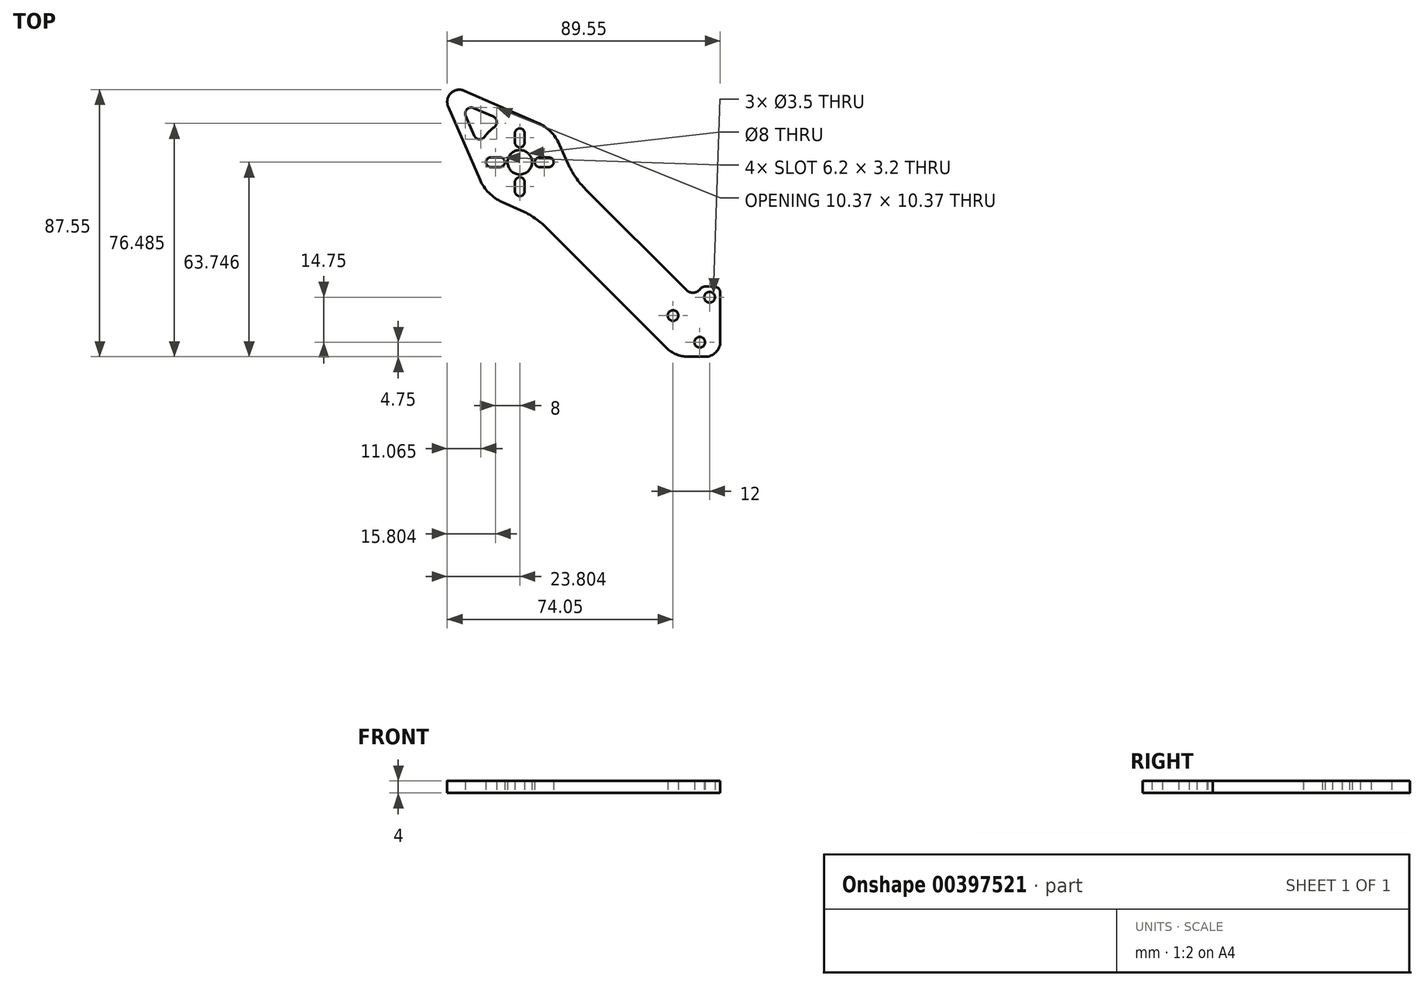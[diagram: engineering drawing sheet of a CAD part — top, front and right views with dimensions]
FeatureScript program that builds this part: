
annotation { "Feature Type Name" : "Feature", "Feature Type Description" : "" }
export const myFeature = defineFeature(function(context is Context, id is Id, definition is map)
    precondition{}
    {
        {
            var Q0;
            Q0=qCreatedBy(makeId("Top.planeOp"),FACE);
            var sketch = newSketch(context, id + "F0", { "sketchPlane" : qUnion([Q0])});
            skCircle(sketch, "E0", {"center": v(0, 0) * mm, "radius": 105 * mm, "construction": true});
            skCircle(sketch, "E1", {"center": v(-15.25, 15.25) * mm, "radius": 1.75 * mm});
            skLineSegment(sketch, "E2", {"start": v(-19.09, 10.5) * mm, "end": v(-13.5, 10.5) * mm});
            skCircle(sketch, "E3", {"center": v(-24, 24) * mm, "radius": 1.75 * mm});
            skLineSegment(sketch, "E4", {"start": v(0, 0) * mm, "end": v(-74.25, 74.25) * mm, "construction": true});
            skLineSegment(sketch, "E5", {"start": v(-65.32, 52.6) * mm, "end": v(-26.16, 13.43) * mm});
            skLineSegment(sketch, "E6", {"start": v(-52.6, 65.32) * mm, "end": v(-19.63, 32.36) * mm});
            skPoint(sketch, "E7.visualSharp", {"position": v(-23.23, 10.5) * mm});
            skArc(sketch, "E7.filletArc", {"start": v(-26.16, 13.43) * mm, "mid": v(-22.91, 11.26) * mm, "end": v(-19.09, 10.5) * mm});
            skCircle(sketch, "E8", {"center": v(-74.25, 74.25) * mm, "radius": 4 * mm});
            skArc(sketch, "E9", {"start": v(-87.31, 68.56) * mm, "mid": v(-84.37, 64.22) * mm, "end": v(-80.06, 61.24) * mm});
            skArc(sketch, "E10", {"start": v(-92.45, 97.71) * mm, "mid": v(-96.87, 96.87) * mm, "end": v(-97.71, 92.45) * mm});
            skLineSegment(sketch, "E11", {"start": v(-94.05, 94.05) * mm, "end": v(-74.25, 74.25) * mm, "construction": true});
            skLineSegment(sketch, "E12", {"start": v(-92.45, 97.71) * mm, "end": v(-68.56, 87.31) * mm});
            skLineSegment(sketch, "E13", {"start": v(-87.31, 68.56) * mm, "end": v(-97.71, 92.45) * mm});
            skLineSegment(sketch, "E14", {"start": v(-61.24, 80.06) * mm, "end": v(-58.46, 73.85) * mm});
            skLineSegment(sketch, "E15", {"start": v(-80.06, 61.24) * mm, "end": v(-73.85, 58.46) * mm});
            skArc(sketch, "E16.trimOffspring", {"start": v(-61.24, 80.06) * mm, "mid": v(-64.22, 84.37) * mm, "end": v(-68.56, 87.31) * mm});
            skPoint(sketch, "E17.center.orphan", {"position": v(-54.45, 54.45) * mm});
            skLineSegment(sketch, "E18", {"start": v(-74.25, 74.25) * mm, "end": v(-74.25, 80.75) * mm, "construction": true});
            skLineSegment(sketch, "E19", {"start": v(-74.25, 80.75) * mm, "end": v(-74.25, 83.75) * mm, "construction": true});
            skLineSegment(sketch, "E20.1.0", {"start": v(-80.75, 74.25) * mm, "end": v(-83.75, 74.25) * mm, "construction": true});
            skLineSegment(sketch, "E20.2.0", {"start": v(-74.25, 67.75) * mm, "end": v(-74.25, 64.75) * mm, "construction": true});
            skLineSegment(sketch, "E20.3.0", {"start": v(-67.75, 74.25) * mm, "end": v(-64.75, 74.25) * mm, "construction": true});
            skArc(sketch, "E21.0.startCap", {"start": v(-72.65, 80.75) * mm, "mid": v(-74.25, 79.15) * mm, "end": v(-75.85, 80.75) * mm});
            skArc(sketch, "E21.0.endCap", {"start": v(-75.85, 83.75) * mm, "mid": v(-74.25, 85.35) * mm, "end": v(-72.65, 83.75) * mm});
            skLineSegment(sketch, "E21.0.left", {"start": v(-75.85, 80.75) * mm, "end": v(-75.85, 83.75) * mm});
            skLineSegment(sketch, "E21.0.right", {"start": v(-72.65, 80.75) * mm, "end": v(-72.65, 83.75) * mm});
            skArc(sketch, "E22.0.startCap", {"start": v(-80.75, 75.85) * mm, "mid": v(-79.15, 74.25) * mm, "end": v(-80.75, 72.65) * mm});
            skArc(sketch, "E22.0.endCap", {"start": v(-83.75, 72.65) * mm, "mid": v(-85.35, 74.25) * mm, "end": v(-83.75, 75.85) * mm});
            skLineSegment(sketch, "E22.0.left", {"start": v(-80.75, 72.65) * mm, "end": v(-83.75, 72.65) * mm});
            skLineSegment(sketch, "E22.0.right", {"start": v(-80.75, 75.85) * mm, "end": v(-83.75, 75.85) * mm});
            skArc(sketch, "E22.1.startCap", {"start": v(-75.85, 67.75) * mm, "mid": v(-74.25, 69.35) * mm, "end": v(-72.65, 67.75) * mm});
            skArc(sketch, "E22.1.endCap", {"start": v(-72.65, 64.75) * mm, "mid": v(-74.25, 63.15) * mm, "end": v(-75.85, 64.75) * mm});
            skLineSegment(sketch, "E22.1.left", {"start": v(-72.65, 67.75) * mm, "end": v(-72.65, 64.75) * mm});
            skLineSegment(sketch, "E22.1.right", {"start": v(-75.85, 67.75) * mm, "end": v(-75.85, 64.75) * mm});
            skArc(sketch, "E22.2.startCap", {"start": v(-67.75, 72.65) * mm, "mid": v(-69.35, 74.25) * mm, "end": v(-67.75, 75.85) * mm});
            skArc(sketch, "E22.2.endCap", {"start": v(-64.75, 75.85) * mm, "mid": v(-63.15, 74.25) * mm, "end": v(-64.75, 72.65) * mm});
            skLineSegment(sketch, "E22.2.left", {"start": v(-67.75, 75.85) * mm, "end": v(-64.75, 75.85) * mm});
            skLineSegment(sketch, "E22.2.right", {"start": v(-67.75, 72.65) * mm, "end": v(-64.75, 72.65) * mm});
            skArc(sketch, "E23", {"start": v(-82.61, 85.78) * mm, "mid": v(-84.32, 84.32) * mm, "end": v(-85.78, 82.61) * mm});
            skLineSegment(sketch, "E24.0", {"start": v(-89.23, 83) * mm, "end": v(-92.02, 89.38) * mm});
            skLineSegment(sketch, "E25.0", {"start": v(-89.38, 92.02) * mm, "end": v(-83, 89.23) * mm});
            skArc(sketch, "E26.filletArc", {"start": v(-89.38, 92.02) * mm, "mid": v(-91.6, 91.6) * mm, "end": v(-92.02, 89.38) * mm});
            skPoint(sketch, "E27.visualSharp", {"position": v(-87.6, 79.23) * mm});
            skArc(sketch, "E27.filletArc", {"start": v(-89.23, 83) * mm, "mid": v(-87.62, 81.8) * mm, "end": v(-85.78, 82.61) * mm});
            skPoint(sketch, "E28.visualSharp", {"position": v(-79.23, 87.6) * mm});
            skArc(sketch, "E28.filletArc", {"start": v(-82.61, 85.78) * mm, "mid": v(-81.8, 87.62) * mm, "end": v(-83, 89.23) * mm});
            skPoint(sketch, "E29.visualSharp", {"position": v(-69.04, 56.31) * mm});
            skArc(sketch, "E29.filletArc", {"start": v(-65.32, 52.6) * mm, "mid": v(-69.31, 55.92) * mm, "end": v(-73.85, 58.46) * mm});
            skPoint(sketch, "E30.visualSharp", {"position": v(-56.31, 69.04) * mm});
            skArc(sketch, "E30.filletArc", {"start": v(-58.46, 73.85) * mm, "mid": v(-55.92, 69.31) * mm, "end": v(-52.6, 65.32) * mm});
            skLineSegment(sketch, "E31", {"start": v(-8.5, 15.5) * mm, "end": v(-8.5, 31.5) * mm});
            skLineSegment(sketch, "E32", {"start": v(-10.5, 33.5) * mm, "end": v(-13.5, 33.5) * mm});
            skLineSegment(sketch, "E33", {"start": v(-15.5, 31.5) * mm, "end": v(-15.5, 30.5) * mm, "construction": true});
            skCircle(sketch, "E34", {"center": v(-12, 30) * mm, "radius": 1.75 * mm});
            skPoint(sketch, "E35.visualSharp", {"position": v(-15.5, 28.23) * mm});
            skPoint(sketch, "E36.visualSharp", {"position": v(-15.5, 33.5) * mm});
            skArc(sketch, "E36.filletArc", {"start": v(-13.5, 33.5) * mm, "mid": v(-14.4, 33.29) * mm, "end": v(-15.1, 32.7) * mm});
            skPoint(sketch, "E37.visualSharp", {"position": v(-8.5, 33.5) * mm});
            skArc(sketch, "E37.filletArc", {"start": v(-8.5, 31.5) * mm, "mid": v(-9.09, 32.91) * mm, "end": v(-10.5, 33.5) * mm});
            skPoint(sketch, "E38.visualSharp", {"position": v(-8.5, 10.5) * mm});
            skArc(sketch, "E38.filletArc", {"start": v(-13.5, 10.5) * mm, "mid": v(-9.96, 11.96) * mm, "end": v(-8.5, 15.5) * mm});
            skArc(sketch, "E39", {"start": v(-19.63, 32.36) * mm, "mid": v(-17.3, 31.5) * mm, "end": v(-15.1, 32.7) * mm});
            skSolve(sketch);
        }
        {
            var Q0;
            Q0=makeQuery(id+"F0.imprint","IMPRINT",FACE,{"disambiguationData":[TD([[makeQuery(id+"F0.imprint","IMPRINT",EDGE,{"derivedFrom":sQuery(id+"F0.wireOp",EDGE,"E1")}),-1.0]])]});
            extrude(context, id + "F1", {"entities" : qUnion([Q0]), "depth" : 4 * mm});
        }
    });
